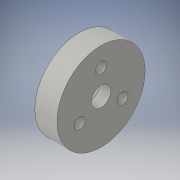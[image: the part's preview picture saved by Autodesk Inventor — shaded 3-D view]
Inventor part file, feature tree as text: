
AUTODESK INVENTOR PART (.ipt)
format: ipt  version: 2016 (Build 200138000, 138)  size: 120,832 bytes
history: native  units: in
note: dims shown in document units (in); Inventor stores cm internally (conversion verified against a paired STEP export)
features: sketch x2, revolve x1, hole x1
ambient origin geometry x8: Origin, YZ Plane, XZ Plane, XY Plane, X Axis, Y Axis, Z Axis, Center Point
bodies: Solid1 (feature_tree)
feature tree (4):
  revolve  "Revolution1"  [1 undecoded]
  hole  "Hole1"  [1 undecoded]
  sketch  "Sketch1"  dims[d0=4.0in d1=0.44in]
  sketch  "Sketch2"  dims[d2=2.0in d3=0.25in d4=1.0in d5=0.5in d6=2.8121in d7=90.0deg d8=2.25in d9=1.1811in d11=360.0deg d13=0.5in d14=0.75in d15=0.375in d16=0.25in d17=0.5635in d18=1.0in d19=0.8108in]
note: 2 required parameter values undecoded (feature->parameter linkage not recoverable at this tier; creation-order binding heuristic only, values carry confidence <= 0.55)